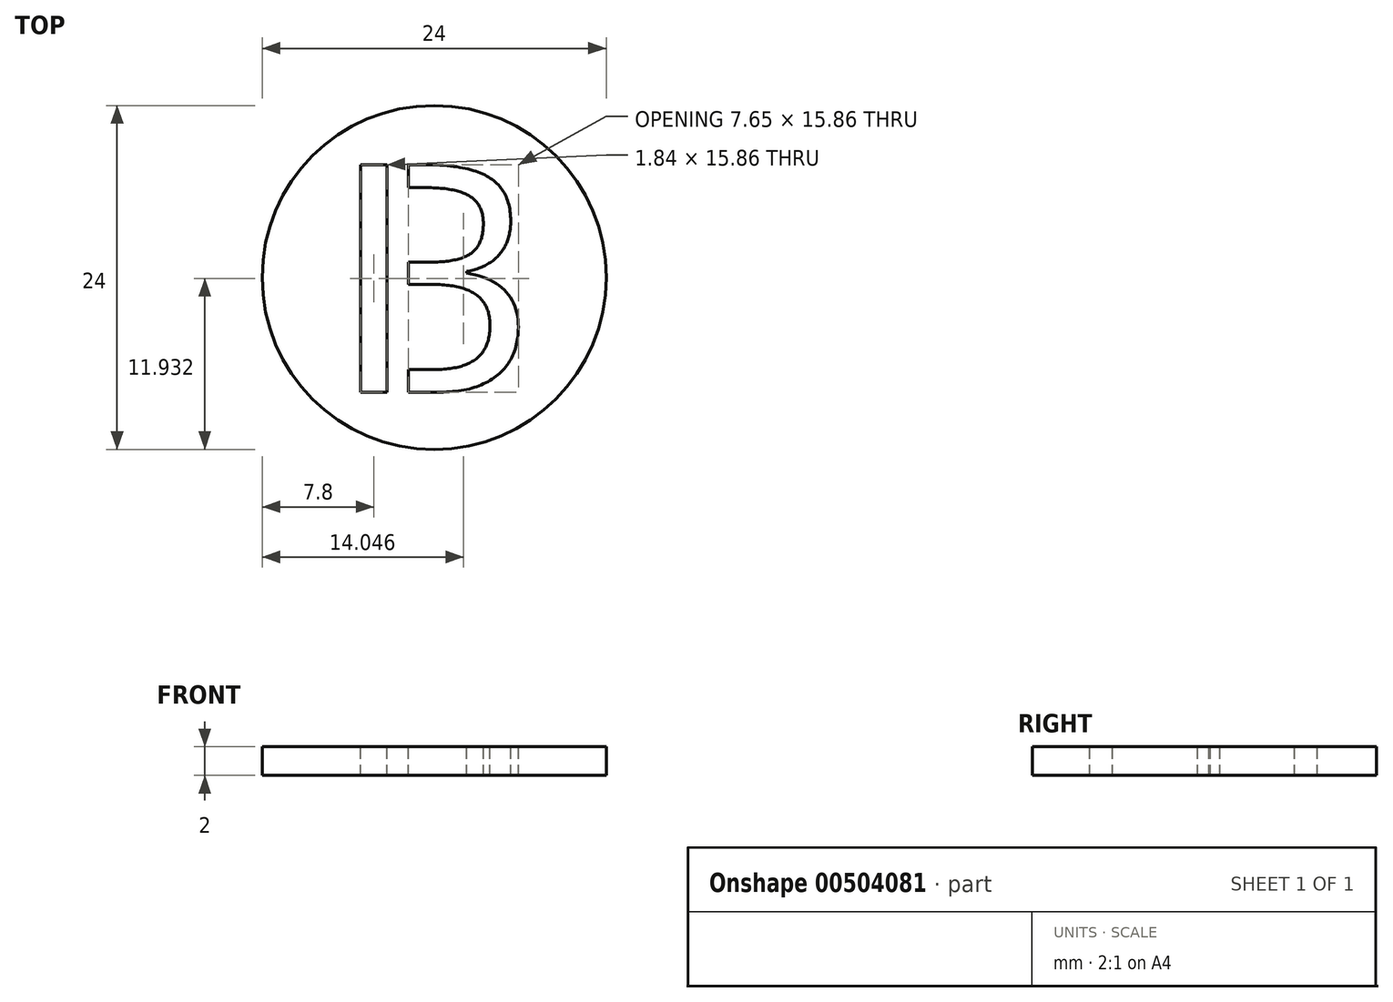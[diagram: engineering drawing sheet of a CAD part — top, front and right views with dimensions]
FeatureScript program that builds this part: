
annotation { "Feature Type Name" : "Feature", "Feature Type Description" : "" }
export const myFeature = defineFeature(function(context is Context, id is Id, definition is map)
    precondition{}
    {
        {
            var Q0;
            Q0=qCreatedBy(makeId("Top.planeOp"),FACE);
            var sketch = newSketch(context, id + "F0", { "sketchPlane" : qUnion([Q0])});
            skCircle(sketch, "E0", {"center": v(0, 0) * mm, "radius": 12 * mm});
            skSolve(sketch);
        }
        {
            var Q0;
            Q0=qSketchRegion(id+"F0",true);
            extrude(context, id + "F1", {"entities" : qUnion([Q0]), "depth" : 2 * mm});
        }
        {
            var Q0;
            Q0=makeQuery(id+"F1.opExtrude","CAP_FACE",FACE,{"disambiguationData":[OSD([sQuery(id+"F0.wireOp",EDGE,"E0")])],"isStart":false});
            var sketch = newSketch(context, id + "F2", { "sketchPlane" : qUnion([Q0])});
            skText(sketch, "E1", { "text": "B", "fontName": "OpenSans-Regular.ttf"});
            skPoint(sketch, "E2", {"position": v(7.3, 0) * mm});
            skPoint(sketch, "E3", {"position": v(-3.28, 3.83) * mm});
            skLineSegment(sketch, "E4", {"start": v(-3.28, 3.83) * mm, "end": v(-1.78, 3.83) * mm, "construction": true});
            skLineSegment(sketch, "E5.bottom", {"start": v(-3.28, 8) * mm, "end": v(-1.78, 8) * mm});
            skLineSegment(sketch, "E5.top", {"start": v(-3.28, -8) * mm, "end": v(-1.78, -8) * mm});
            skLineSegment(sketch, "E5.left", {"start": v(-3.28, 8) * mm, "end": v(-3.28, -8) * mm});
            skLineSegment(sketch, "E5.right", {"start": v(-1.78, 8) * mm, "end": v(-1.78, -8) * mm});
            const initialGuessF2  = {"E1": [-0.0073, -0.008, 1, 0, 0.016]};
            skSetInitialGuess(sketch, initialGuessF2);
            skSolve(sketch);
        }
        {
            var Q0;
            {var subQ8=sQuery(id+"F2.wireOp",EDGE,"E1.sketch_text.stroke-10");Q0=makeQuery(id+"F2.imprint","IMPRINT",FACE,{"disambiguationData":[TD([[makeQuery(id+"F2.imprint","IMPRINT",EDGE,{"derivedFrom":subQ8}),-1.0]])]});}
            var Q1;
            {var subQ10=sQuery(id+"F2.wireOp",EDGE,"E1.sketch_text.stroke-1");Q1=makeQuery(id+"F2.imprint","IMPRINT",FACE,{"disambiguationData":[TD([[makeQuery(id+"F2.imprint","IMPRINT",EDGE,{"derivedFrom":subQ10}),-1.0]])]});}
            extrude(context, id + "F3", {"entities" : qUnion([Q0, Q1]), "operationType" : NewBodyOperationType.REMOVE, "oppositeDirection" : true, "depth" : 25 * mm, "offsetDistance" : 25 * mm});
        }
    });
